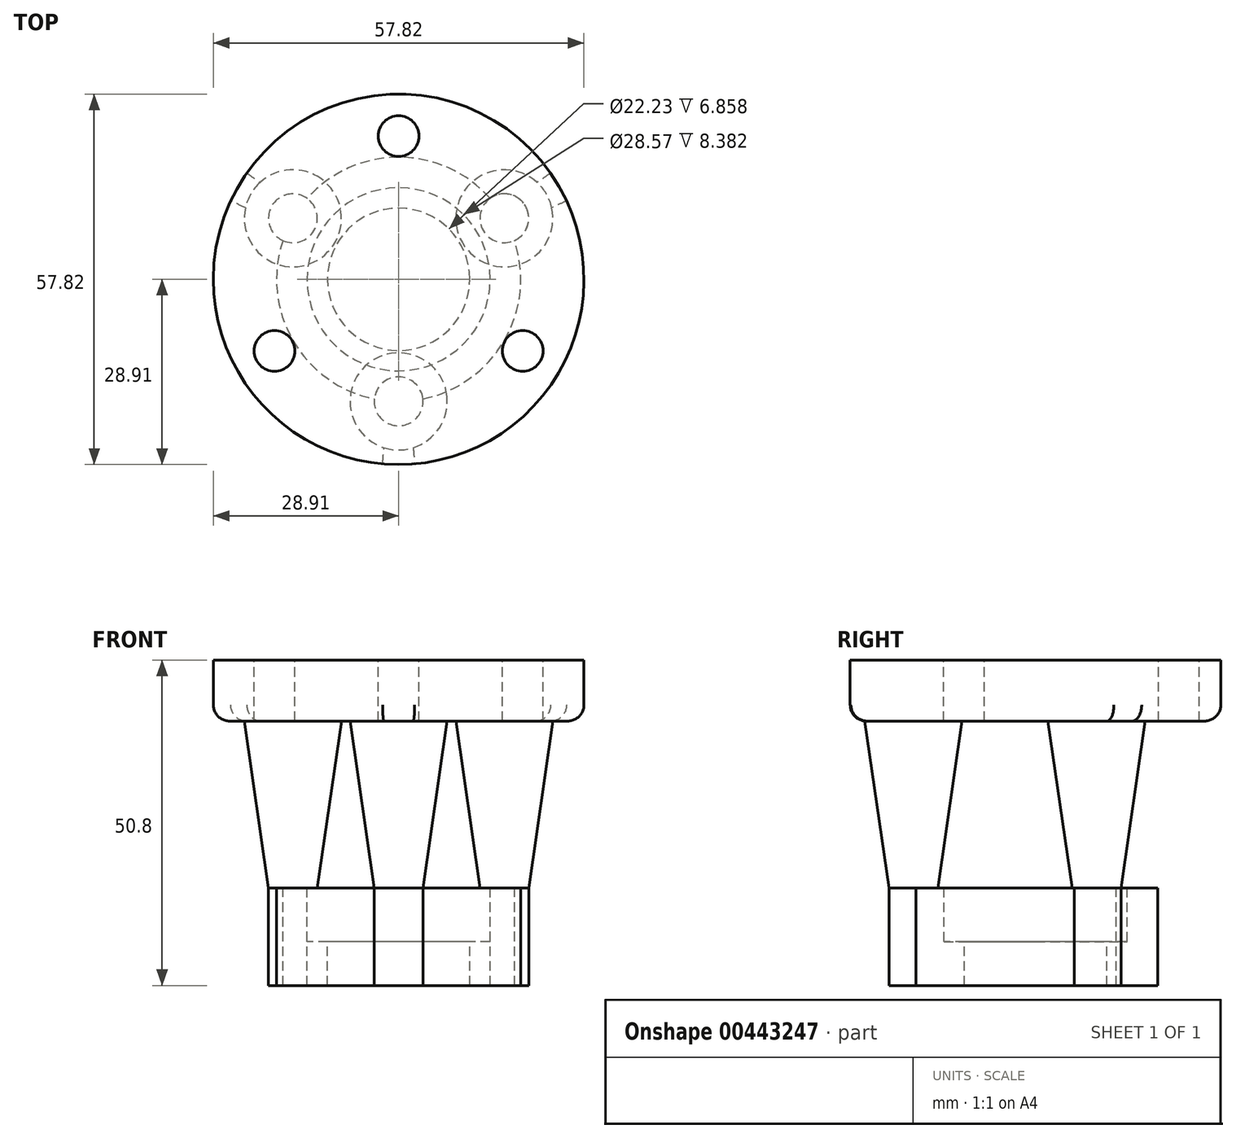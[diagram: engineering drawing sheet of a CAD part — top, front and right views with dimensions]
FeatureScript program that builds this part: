
annotation { "Feature Type Name" : "Feature", "Feature Type Description" : "" }
export const myFeature = defineFeature(function(context is Context, id is Id, definition is map)
    precondition{}
    {
        {
            var Q0;
            Q0=qCreatedBy(makeId("Top.planeOp"),FACE);
            var sketch = newSketch(context, id + "F0", { "sketchPlane" : qUnion([Q0])});
            skCircle(sketch, "E0", {"center": v(0, 0) * mm, "radius": 11.11 * mm});
            skCircle(sketch, "E1", {"center": v(0, 0) * mm, "radius": 14.29 * mm});
            skCircle(sketch, "E2", {"center": v(0, -19.05) * mm, "radius": 3.81 * mm});
            skCircle(sketch, "E3.1.0", {"center": v(16.5, 9.52) * mm, "radius": 3.81 * mm});
            skCircle(sketch, "E3.2.0", {"center": v(-16.5, 9.53) * mm, "radius": 3.81 * mm});
            skArc(sketch, "E4", {"start": v(-14.27, 12.62) * mm, "mid": v(-16.5, 9.53) * mm, "end": v(-18.06, 6.05) * mm, "construction": true});
            skArc(sketch, "E5", {"start": v(-18.06, 6.05) * mm, "mid": v(-16.5, -9.53) * mm, "end": v(-3.8, -18.67) * mm});
            skArc(sketch, "E6", {"start": v(14.27, 12.62) * mm, "mid": v(0, 19.05) * mm, "end": v(-14.27, 12.62) * mm});
            skArc(sketch, "E7", {"start": v(18.06, 6.05) * mm, "mid": v(16.5, 9.52) * mm, "end": v(14.27, 12.62) * mm, "construction": true});
            skArc(sketch, "E8", {"start": v(3.8, -18.67) * mm, "mid": v(16.5, -9.53) * mm, "end": v(18.06, 6.05) * mm});
            skArc(sketch, "E9", {"start": v(-3.8, -18.67) * mm, "mid": v(0, -19.05) * mm, "end": v(3.8, -18.67) * mm, "construction": true});
            skSolve(sketch);
        }
        {
            var Q0;
            Q0=makeQuery(id+"F0.imprint","IMPRINT",FACE,{"disambiguationData":[TD([[makeQuery(id+"F0.imprint","IMPRINT",EDGE,{"derivedFrom":sQuery(id+"F0.wireOp",EDGE,"E1")}),-1.0]])]});
            var Q1;
            Q1=makeQuery(id+"F0.imprint","IMPRINT",FACE,{"disambiguationData":[TD([[makeQuery(id+"F0.imprint","IMPRINT",EDGE,{"derivedFrom":sQuery(id+"F0.wireOp",EDGE,"E0")}),-1.0]])]});
            var Q2;
            {var subQ0=sQuery(id+"F0.wireOp",EDGE,"E3.2.0");var subQ1=sQuery(id+"F0.wireOp",EDGE,"aioWRYlR-4Btv-0cnh-m9kv-mFUz9vxmGDX2");var subQ2=makeQuery(id+"F0.imprint","INTERSECT",VERTEX,{"disambiguationData":[OD(0.0)],"derivedFrom":[subQ1,subQ0]});Q2=makeQuery(id+"F0.imprint","IMPRINT",FACE,{"disambiguationData":[TD([[makeQuery(id+"F0.imprint","IMPRINT",EDGE,{"disambiguationData":[TD([[subQ2,-1.0]])],"derivedFrom":subQ1}),1.0]])]});}
            var Q3;
            {var subQ0=sQuery(id+"F0.wireOp",EDGE,"E3.1.0");var subQ1=sQuery(id+"F0.wireOp",EDGE,"aioWRYlR-4Btv-0cnh-m9kv-mFUz9vxmGDX2");var subQ2=makeQuery(id+"F0.imprint","INTERSECT",VERTEX,{"disambiguationData":[OD(0.0)],"derivedFrom":[subQ1,subQ0]});Q3=makeQuery(id+"F0.imprint","IMPRINT",FACE,{"disambiguationData":[TD([[makeQuery(id+"F0.imprint","IMPRINT",EDGE,{"disambiguationData":[TD([[subQ2,1.0]])],"derivedFrom":subQ1}),1.0]])]});}
            var Q4;
            {var subQ0=sQuery(id+"F0.wireOp",EDGE,"E2");var subQ1=sQuery(id+"F0.wireOp",EDGE,"aioWRYlR-4Btv-0cnh-m9kv-mFUz9vxmGDX2");var subQ2=makeQuery(id+"F0.imprint","INTERSECT",VERTEX,{"disambiguationData":[OD(0.0)],"derivedFrom":[subQ1,subQ0]});Q4=makeQuery(id+"F0.imprint","IMPRINT",FACE,{"disambiguationData":[TD([[makeQuery(id+"F0.imprint","IMPRINT",EDGE,{"disambiguationData":[TD([[subQ2,-1.0]])],"derivedFrom":subQ1}),1.0]])]});}
            var Q5;
            {var subQ0=sQuery(id+"F0.wireOp",EDGE,"E2");var subQ1=sQuery(id+"F0.wireOp",EDGE,"aioWRYlR-4Btv-0cnh-m9kv-mFUz9vxmGDX2");var subQ2=makeQuery(id+"F0.imprint","INTERSECT",VERTEX,{"disambiguationData":[OD(0.0)],"derivedFrom":[subQ1,subQ0]});Q5=makeQuery(id+"F0.imprint","IMPRINT",FACE,{"disambiguationData":[TD([[makeQuery(id+"F0.imprint","IMPRINT",EDGE,{"disambiguationData":[TD([[subQ2,-1.0]])],"derivedFrom":subQ1}),-1.0]])]});}
            var Q6;
            {var subQ0=sQuery(id+"F0.wireOp",EDGE,"E3.2.0");var subQ1=sQuery(id+"F0.wireOp",EDGE,"aioWRYlR-4Btv-0cnh-m9kv-mFUz9vxmGDX2");var subQ2=makeQuery(id+"F0.imprint","INTERSECT",VERTEX,{"disambiguationData":[OD(0.0)],"derivedFrom":[subQ1,subQ0]});Q6=makeQuery(id+"F0.imprint","IMPRINT",FACE,{"disambiguationData":[TD([[makeQuery(id+"F0.imprint","IMPRINT",EDGE,{"disambiguationData":[TD([[subQ2,-1.0]])],"derivedFrom":subQ1}),-1.0]])]});}
            var Q7;
            {var subQ0=sQuery(id+"F0.wireOp",EDGE,"E3.1.0");var subQ1=sQuery(id+"F0.wireOp",EDGE,"aioWRYlR-4Btv-0cnh-m9kv-mFUz9vxmGDX2");var subQ2=makeQuery(id+"F0.imprint","INTERSECT",VERTEX,{"disambiguationData":[OD(0.0)],"derivedFrom":[subQ1,subQ0]});Q7=makeQuery(id+"F0.imprint","IMPRINT",FACE,{"disambiguationData":[TD([[makeQuery(id+"F0.imprint","IMPRINT",EDGE,{"disambiguationData":[TD([[subQ2,1.0]])],"derivedFrom":subQ1}),-1.0]])]});}
            var Q8;
            {var subQ0=sQuery(id+"F0.wireOp",EDGE,"E3.2.0");var subQ1=makeQuery(id+"F0.imprint","INTERSECT",VERTEX,{"derivedFrom":[subQ0,sQuery(id+"F0.wireOp",EDGE,"E5")]});Q8=makeQuery(id+"F0.imprint","IMPRINT",FACE,{"disambiguationData":[TD([[makeQuery(id+"F0.imprint","IMPRINT",EDGE,{"disambiguationData":[TD([[subQ1,-1.0]])],"derivedFrom":subQ0}),1.0]])]});}
            var Q9;
            {var subQ0=sQuery(id+"F0.wireOp",EDGE,"E3.1.0");var subQ1=makeQuery(id+"F0.imprint","INTERSECT",VERTEX,{"derivedFrom":[subQ0,sQuery(id+"F0.wireOp",EDGE,"E6")]});Q9=makeQuery(id+"F0.imprint","IMPRINT",FACE,{"disambiguationData":[TD([[makeQuery(id+"F0.imprint","IMPRINT",EDGE,{"disambiguationData":[TD([[subQ1,-1.0]])],"derivedFrom":subQ0}),1.0]])]});}
            var Q10;
            {var subQ0=sQuery(id+"F0.wireOp",EDGE,"E2");var subQ1=makeQuery(id+"F0.imprint","INTERSECT",VERTEX,{"derivedFrom":[subQ0,sQuery(id+"F0.wireOp",EDGE,"E5")]});Q10=makeQuery(id+"F0.imprint","IMPRINT",FACE,{"disambiguationData":[TD([[makeQuery(id+"F0.imprint","IMPRINT",EDGE,{"disambiguationData":[TD([[subQ1,1.0]])],"derivedFrom":subQ0}),1.0]])]});}
            extrude(context, id + "F1", {"entities" : qUnion([Q0, Q1, Q2, Q3, Q4, Q5, Q6, Q7, Q8, Q9, Q10]), "oppositeDirection" : true, "depth" : 15.24 * mm});
        }
        {
            var Q0;
            Q0=makeQuery(id+"F0.imprint","IMPRINT",FACE,{"disambiguationData":[TD([[makeQuery(id+"F0.imprint","IMPRINT",EDGE,{"derivedFrom":sQuery(id+"F0.wireOp",EDGE,"E0")}),-1.0]])]});
            extrude(context, id + "F2", {"entities" : qUnion([Q0]), "operationType" : NewBodyOperationType.REMOVE, "oppositeDirection" : true, "depth" : 8.38 * mm});
        }
        {
            var Q0;
            Q0=makeQuery(id+"F1.opExtrude","CAP_FACE",FACE,{"disambiguationData":[OSD([sQuery(id+"F0.wireOp",EDGE,"E0"),sQuery(id+"F0.wireOp",EDGE,"aioWRYlR-4Btv-0cnh-m9kv-mFUz9vxmGDX2")])],"isStart":false});
            cPlane(context, id + "F3", {"entities" : qUnion([Q0]), "cplaneType" : CPlaneType.OFFSET, "offset" : 50.8 * mm, "oppositeDirection" : true, "width" : 152.4 * mm, "height" : 152.4 * mm});
        }
        {
            var Q0;
            Q0=qCreatedBy(id+"F3.planeOp",FACE);
            var sketch = newSketch(context, id + "F4", { "sketchPlane" : qUnion([Q0])});
            skCircle(sketch, "E10", {"center": v(0, 0) * mm, "radius": 28.91 * mm});
            skCircle(sketch, "E11", {"center": v(0, -22.35) * mm, "radius": 3.18 * mm});
            skCircle(sketch, "E12.1.0", {"center": v(19.36, 11.18) * mm, "radius": 3.18 * mm});
            skCircle(sketch, "E12.2.0", {"center": v(-19.36, 11.18) * mm, "radius": 3.18 * mm});
            skSolve(sketch);
        }
        {
            var Q0;
            Q0=makeQuery(id+"F4.imprint","IMPRINT",FACE,{"disambiguationData":[TD([[makeQuery(id+"F4.imprint","IMPRINT",EDGE,{"derivedFrom":sQuery(id+"F4.wireOp",EDGE,"E10")}),1.0]])]});
            extrude(context, id + "F5", {"entities" : qUnion([Q0]), "depth" : 9.52 * mm});
        }
        {
            var Q0;
            Q0=makeQuery(id+"F5.opExtrude","CAP_FACE",FACE,{"disambiguationData":[OSD([sQuery(id+"F4.wireOp",EDGE,"E10"),sQuery(id+"F4.wireOp",EDGE,"E11"),sQuery(id+"F4.wireOp",EDGE,"E12.1.0"),sQuery(id+"F4.wireOp",EDGE,"E12.2.0")])],"isStart":false});
            var sketch = newSketch(context, id + "F6", { "sketchPlane" : qUnion([Q0])});
            skPoint(sketch, "E13.0", {"position": v(0, 19.05) * mm});
            skCircle(sketch, "E14", {"center": v(0, 19.05) * mm, "radius": 7.58 * mm});
            skCircle(sketch, "E15.1.0", {"center": v(-16.5, -9.52) * mm, "radius": 7.58 * mm});
            skCircle(sketch, "E15.2.0", {"center": v(16.5, -9.53) * mm, "radius": 7.58 * mm});
            skPoint(sketch, "E15.center", {"position": v(0, 0) * mm});
            skSolve(sketch);
        }
        {
            var Q2;
            {var subQ0=sQuery(id+"F0.wireOp",EDGE,"E3.1.0");var subQ1=makeQuery(id+"F0.imprint","INTERSECT",VERTEX,{"derivedFrom":[subQ0,sQuery(id+"F0.wireOp",EDGE,"E6")]});Q2=makeQuery(id+"F0.imprint","IMPRINT",FACE,{"disambiguationData":[TD([[makeQuery(id+"F0.imprint","IMPRINT",EDGE,{"disambiguationData":[TD([[subQ1,-1.0]])],"derivedFrom":subQ0}),1.0]])]});}
            var Q3;
            Q3=makeQuery(id+"F6.imprint","IMPRINT",FACE,{"disambiguationData":[TD([[makeQuery(id+"F6.imprint","IMPRINT",EDGE,{"derivedFrom":sQuery(id+"F6.wireOp",EDGE,"E15.2.0")}),1.0]])]});
            loft(context, id + "F7", {"operationType" : NewBodyOperationType.ADD, "sheetProfilesArray" : [{ "sheetProfileEntities" : qUnion([Q2]) }, { "sheetProfileEntities" : qUnion([Q3]) }]});
        }
        {
            var Q1;
            {var subQ0=sQuery(id+"F0.wireOp",EDGE,"E3.2.0");var subQ1=makeQuery(id+"F0.imprint","INTERSECT",VERTEX,{"derivedFrom":[subQ0,sQuery(id+"F0.wireOp",EDGE,"E5")]});Q1=makeQuery(id+"F0.imprint","IMPRINT",FACE,{"disambiguationData":[TD([[makeQuery(id+"F0.imprint","IMPRINT",EDGE,{"disambiguationData":[TD([[subQ1,-1.0]])],"derivedFrom":subQ0}),1.0]])]});}
            var Q2;
            Q2=makeQuery(id+"F6.imprint","IMPRINT",FACE,{"disambiguationData":[TD([[makeQuery(id+"F6.imprint","IMPRINT",EDGE,{"derivedFrom":sQuery(id+"F6.wireOp",EDGE,"E15.1.0")}),1.0]])]});
            loft(context, id + "F8", {"operationType" : NewBodyOperationType.ADD, "sheetProfilesArray" : [{ "sheetProfileEntities" : qUnion([Q1]) }, { "sheetProfileEntities" : qUnion([Q2]) }]});
        }
        {
            var Q1;
            {var subQ0=sQuery(id+"F0.wireOp",EDGE,"E2");var subQ1=makeQuery(id+"F0.imprint","INTERSECT",VERTEX,{"derivedFrom":[subQ0,sQuery(id+"F0.wireOp",EDGE,"E5")]});Q1=makeQuery(id+"F0.imprint","IMPRINT",FACE,{"disambiguationData":[TD([[makeQuery(id+"F0.imprint","IMPRINT",EDGE,{"disambiguationData":[TD([[subQ1,1.0]])],"derivedFrom":subQ0}),1.0]])]});}
            var Q2;
            Q2=makeQuery(id+"F6.imprint","IMPRINT",FACE,{"disambiguationData":[TD([[makeQuery(id+"F6.imprint","IMPRINT",EDGE,{"derivedFrom":sQuery(id+"F6.wireOp",EDGE,"E14")}),1.0]])]});
            loft(context, id + "F9", {"operationType" : NewBodyOperationType.ADD, "sheetProfilesArray" : [{ "sheetProfileEntities" : qUnion([Q1]) }, { "sheetProfileEntities" : qUnion([Q2]) }]});
        }
        {
            var Q0;
            Q0=makeQuery(id+"F5.opExtrude","CAP_EDGE",EDGE,{"disambiguationData":[OSD([sQuery(id+"F4.wireOp",EDGE,"E10")])],"isStart":false});
            fillet(context, id + "F10", {"entities" : qUnion([Q0]), "radius" : 2.54 * mm, "tangentPropagation" : true, "allowEdgeOverflow" : false});
        }
    });
